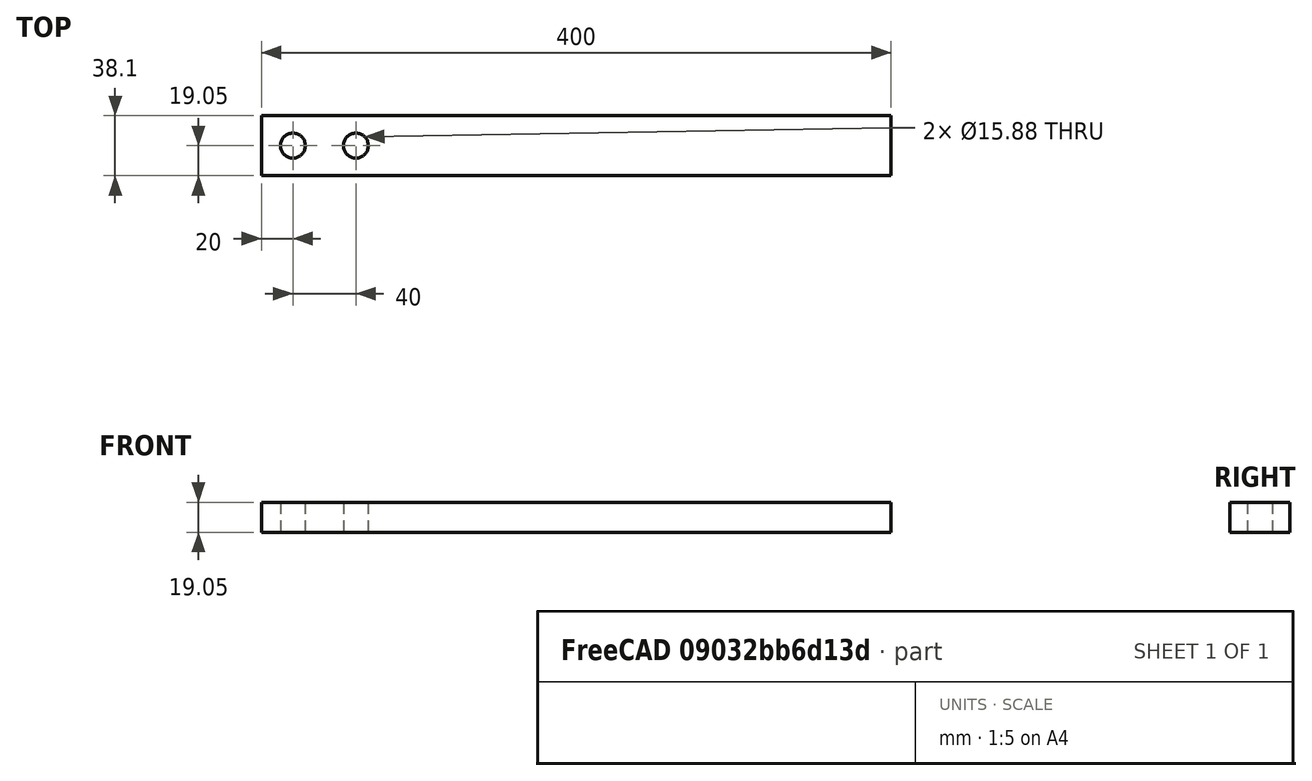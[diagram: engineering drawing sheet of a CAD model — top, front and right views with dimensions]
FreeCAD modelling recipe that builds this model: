
FCSTD DOCUMENT  (FreeCAD 0.19R24291 (Git))
Label: top2
License: All rights reserved
LicenseURL: http://en.wikipedia.org/wiki/All_rights_reserved
objects: Sketcher::SketchObject×1, PartDesign::Pad×1, PartDesign::Body×1
note: 4 computed .brp shape members not serialized (recipe doc carries the construction recipe); baked Part::Feature solids carry a one-line shape summary decoded from their .brp

FEATURE [Sketcher::SketchObject] Sketch
  FullyConstrained = true
  MapMode = 5
  Support = -> [XY_Plane]
  expr: Constraints[10] = 1.5 * 25.4
  expr: Constraints[15] = 1.5 * 25.4 / 2
  sketch-geometry (7):
    g0: LineSegment StartX=0 StartY=0 StartZ=0 EndX=400 EndY=0 EndZ=0
    g1: LineSegment StartX=400 StartY=0 StartZ=0 EndX=400 EndY=38.1 EndZ=0
    g2: LineSegment StartX=400 StartY=38.1 StartZ=0 EndX=0 EndY=38.1 EndZ=0
    g3: LineSegment StartX=0 StartY=38.1 StartZ=0 EndX=0 EndY=0 EndZ=0
    g4: Circle CenterX=20 CenterY=19.05 CenterZ=0 NormalX=0 NormalY=0 NormalZ=1 AngleXU=0 Radius=7.9375
    g5: LineSegment StartX=0 StartY=19.05 StartZ=0 EndX=400 EndY=19.05 EndZ=0
    g6: Circle CenterX=60 CenterY=19.05 CenterZ=0 NormalX=0 NormalY=0 NormalZ=1 AngleXU=0 Radius=7.9375
  constraints (21):
    c: Coincident(g0,g1)
    c: Coincident(g1,g2)
    c: Coincident(g2,g3)
    c: Coincident(g3,g0)
    c: Horizontal(g0)
    c: Horizontal(g2)
    c: Vertical(g1)
    c: Vertical(g3)
    c: Coincident(g0,g-1)
    c: Diameter(g4) = 15.875
    c: DistanceY(g3,g3) = 38.1
    c: DistanceX(g0,g0) = 400
    c: PointOnObject(g5,g3)
    c: PointOnObject(g5,g1)
    c: Horizontal(g5)
    c: DistanceY(g0,g5) = 19.05
    c: PointOnObject(g4,g5)
    c: DistanceX(g5,g4) = 20
    c: Equal(g4,g6) = 15.875
    c: PointOnObject(g6,g5)
    c: DistanceX(g4,g6) = 40
FEATURE [PartDesign::Pad] Pad
  Direction = (1,1,1)
  Length = 19.05
  Length2 = 100
  Profile = -> Sketch
  Type = 0
FEATURE [PartDesign::Body] Body
  Group = -> [Sketch,Pad]
  Origin = -> Origin
  Tip = -> Pad
